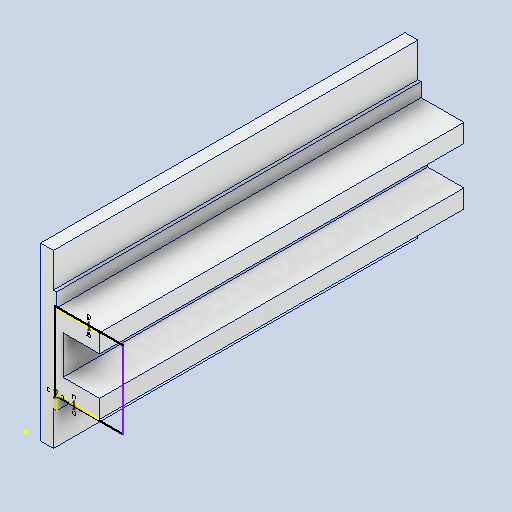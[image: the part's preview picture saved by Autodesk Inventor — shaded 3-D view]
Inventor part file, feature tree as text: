
AUTODESK INVENTOR PART (.ipt)
format: ipt  version: 2024 (Build 280153000, 153)  size: 343,040 bytes
history: native  units: mm
features: sketch x7, extrude x6, projected_geometry x3
ambient origin geometry x8: Origin, YZ Plane, XZ Plane, XY Plane, X Axis, Y Axis, Z Axis, Center Point
bodies: Solid1 (feature_tree)
feature tree (16):
  extrude  "Extrusion1"  Depth=160.0mm TaperAngle=0.0deg
  extrude  "Extrusion2"  Depth=25.0mm
  extrude  "Extrusion3"  Depth=45.0mm
  extrude  "Extrusion4"  Depth=45.0mm
  extrude  "Extrusion5"  Depth=36.0mm
  extrude  "Extrusion6"  Depth=150.0mm TaperAngle=0.0deg
  sketch  "Sketch7"  dims[d15=20.0mm d16=340.0mm d17=200.0mm d18=0.0mm d19=30.0mm d20=0.0mm d21=5.0mm d22=0.0mm d23=13.0mm d24=13.0mm d25=3.0mm d26=500.0mm d27=0.0mm d28=1.0mm d29=1.0mm d30=2.0mm]
  sketch  "Sketch1"  dims[d0=475.0mm d1=160.0mm d2=0.0mm]
  sketch  "Sketch2"  dims[d4=25.0mm d5=25.0mm]
  sketch  "Sketch3"  dims[d6=10.0mm d7=45.0mm]
  sketch  "Sketch4"  dims[d8=45.0mm d9=4.0mm]
  projected_geometry  "Projected Loop1"
  projected_geometry  "Projected Loop2"
  sketch  "Sketch5"  dims[d10=36.0mm d11=80.0mm]
  projected_geometry  "Projected Loop3"
  sketch  "Sketch6"  dims[d12=80.0mm d13=150.0mm d14=0.0mm]
